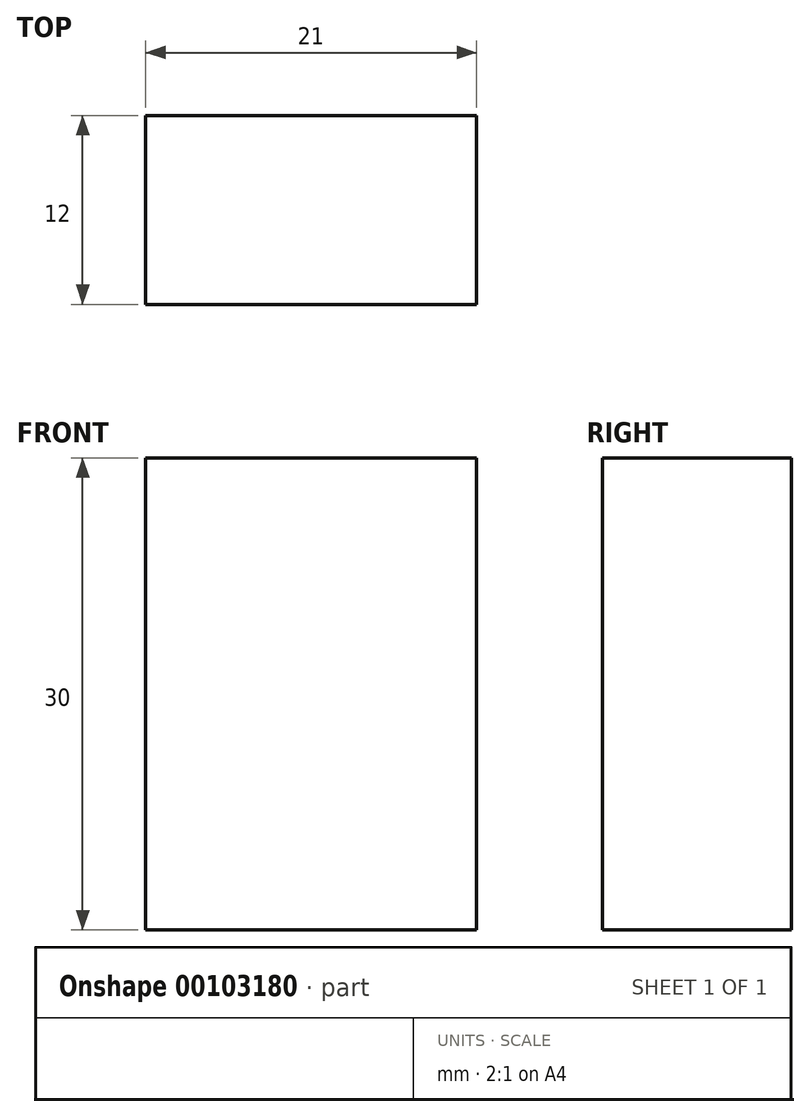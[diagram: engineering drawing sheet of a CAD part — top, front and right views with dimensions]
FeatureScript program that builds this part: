
annotation { "Feature Type Name" : "Feature", "Feature Type Description" : "" }
export const myFeature = defineFeature(function(context is Context, id is Id, definition is map)
    precondition{}
    {
        {
            var Q0;
            Q0=qCreatedBy(makeId("Top.planeOp"),FACE);
            var sketch = newSketch(context, id + "F0", { "sketchPlane" : qUnion([Q0])});
            skLineSegment(sketch, "E0.bottom", {"start": v(10.5, -6) * mm, "end": v(-10.5, -6) * mm});
            skLineSegment(sketch, "E0.top", {"start": v(10.5, 6) * mm, "end": v(-10.5, 6) * mm});
            skLineSegment(sketch, "E0.left", {"start": v(10.5, -6) * mm, "end": v(10.5, 6) * mm});
            skLineSegment(sketch, "E0.right", {"start": v(-10.5, -6) * mm, "end": v(-10.5, 6) * mm});
            skPoint(sketch, "E0.middle", {"position": v(0, 0) * mm});
            skSolve(sketch);
        }
        {
            var Q0;
            Q0 = qSketchRegion(id + "F0", true);
            var Q1;
            Q1=makeQuery(id+"F0.imprint","IMPRINT",FACE,{"disambiguationData":[TD([[makeQuery(id+"F0.imprint","IMPRINT",EDGE,{"derivedFrom":sQuery(id+"F0.wireOp",EDGE,"E0.bottom")}),-1.0]])]});
            extrude(context, id + "F1", {"entities" : qUnion([Q0, Q1]), "depth" : 30 * mm});
        }
    });
